# Revit family: IS_Synergy_Multiproduct_BIM_GB_L6220;L6221;L6222;L6223;L6224;L6225;L6226;L6227
name_source: partatom
category: Plumbing Fixtures
revit_build: Autodesk Revit MEP 2012 (Build: 20110309_2315(x64)
units: mm (PartAtom-declared; Revit-internal decimal feet)

## types (8) — shared parameters
Accessories = www.idealspec.co.uk
AreaUnits = millimeters
Assembly Code = C1030200
AssetType = Fixed
BREEAM = No
Brand = Ideal Standard
CodePerformance = EN 14428:2004
EN 14428:2004
Color = Silver, clear
Default Elevation = 1219 mm
DurationUnit = year
ECA = No
ExpectedLife = 30
Features = Idealclean clear glass, bright silver finish
Finish = Clear, silver
FrameMatl = ISI_IdealStandard_Shower_BrightSilver_Render
GlazingMatl = ISI_IdealStandard_Shower_Glass_Render
IfcExportAs = IfcFurnitureType
IfcExportType = USERDEFINED
InstallationInstructions = www.idealspec.co.uk/resources.html
LinearUnits = millimeters
MainColor = Silver, clear
ManufacturerURL = www.idealspec.co.uk
Material = Glass, aluminium
NBSDescription = Shower enclosures
NBSReference = 45-35-70/332
NominalHeight = 2000 mm  [stored 6.56168 ft]
Shape = Rectangular
Space = Internal
SpareParts = www.fastpart-spares.co.uk
TMV3 = No
URL = www.idealspec.co.uk
Uniclass2 = Pr_40_20_06_79
Version = 1
VolumeUnits = Litres
WRAS = No
WarrantyDescription = Manufacturers warranty
WarrantyDurationParts = 10
WarrantyDurationUnit = year
WaterEfficientProduct = No

## per-type parameters (varying)
| type | BIMObjectName | Description | Model | ModelNumber | ModelReference | Name | NettWeight | NominalDepth | NominalDepthActual | NominalLength | NominalWidth | ProductInformation | Size |
| L6220EO - Synergy wet room panel 700 mm | ISI_IdealStandard_Showers_Synergy-WetRoomPanel_L6220EO | Synergy 700 mm wet room panel | L6220EO | L6220EO | Synergy 700 mm wet room panel | Showers_Synergy-WetRoomPanel_L6220EO_IdealStandard | 26.9 Kg | 700 mm  [stored 2.29659 ft] | 700 mm  [stored 2.29659 ft] | 700 mm  [stored 2.29659 ft] | 700 mm  [stored 2.29659 ft] | www.idealspec.co.uk/datasheets/L6220EO | 2025 x 700 x 50mm |
| L6221EO - Synergy wet room panel 760 mm | ISI_IdealStandard_Showers_Synergy-WetRoomPanel_L6221EO | Synergy 760 mm wet room panel | L6221EO | L6221EO | Synergy 760 mm wet room panel | Showers_Synergy-WetRoomPanel_L6221EO_IdealStandard | 32 Kg | 760 mm | 760 mm | 760 mm | 760 mm | www.idealspec.co.uk/datasheets/L6221EO | 2025 x 760 x 50mm |
| L6222EO - Synergy wet room panel 800 mm | ISI_IdealStandard_Showers_Synergy-WetRoomPanel_L6222EO | Synergy 800 mm wet room panel | L6222EO | L6222EO | Synergy 800 mm wet room panel | Showers_Synergy-WetRoomPanel_L6222EO_IdealStandard | 34 Kg | 800 mm  [stored 2.62467 ft] | 800 mm  [stored 2.62467 ft] | 800 mm  [stored 2.62467 ft] | 800 mm  [stored 2.62467 ft] | www.idealspec.co.uk/datasheets/L6222EO | 2025 x 800 x 50mm |
| L6223EO - Synergy wet room panel 900 mm | ISI_IdealStandard_Showers_Synergy-WetRoomPanel_L6223EO | Synergy 900 mm wet room panel | L6223EO | L6223EO | Synergy 900 mm wet room panel | Showers_Synergy-WetRoomPanel_L6223EO_IdealStandard | 37 Kg | 900 mm  [stored 2.95276 ft] | 900 mm  [stored 2.95276 ft] | 900 mm  [stored 2.95276 ft] | 900 mm  [stored 2.95276 ft] | www.idealspec.co.uk/datasheets/L6223EO | 2025 x 900 x 50mm |
| L6224EO - Synergy wet room panel 1000 mm | ISI_IdealStandard_Showers_Synergy-WetRoomPanel_L6224EO | Synergy 1000 mm wet room panel | L6224EO | L6224EO | Synergy 1000 mm wet room panel | Showers_Synergy-WetRoomPanel_L6224EO_IdealStandard | 42 Kg | 900 mm  [stored 2.95276 ft] | 900 mm  [stored 2.95276 ft] | 900 mm  [stored 2.95276 ft] | 1000 mm  [stored 3.28084 ft] | www.idealspec.co.uk/datasheets/L6224EO | 2025 x 1000 x 50mm |
| L6225EO - Synergy wet room panel 1200 mm | ISI_IdealStandard_Showers_Synergy-WetRoomPanel_L6225EO | Synergy 1200 mm wet room panel | L6225EO | L6225EO | Synergy 1200 mm wet room panel | Showers_Synergy-WetRoomPanel_L6225EO_IdealStandard | 42 Kg | 900 mm  [stored 2.95276 ft] | 900 mm  [stored 2.95276 ft] | 900 mm  [stored 2.95276 ft] | 1200 mm | www.idealspec.co.uk/datasheets/L6225EO | 2025 x 1200 x 50mm |
| L6226EO - Synergy wet room panel 1400 mm | ISI_IdealStandard_Showers_Synergy-WetRoomPanel_L6226EO | Synergy 1400 mm wet room panel | L6226EO | L6226EO | Synergy 1400 mm wet room panel | Showers_Synergy-WetRoomPanel_L6226EO_IdealStandard | 61 Kg | 900 mm  [stored 2.95276 ft] | 900 mm  [stored 2.95276 ft] | 900 mm  [stored 2.95276 ft] | 1400 mm  [stored 4.59318 ft] | www.idealspec.co.uk/datasheets/L6226EO | 2025 x 1400 x 50mm |
| L6227EO - Synergy wet room panel 1600 mm | ISI_IdealStandard_Showers_Synergy-WetRoomPanel_L6227EO | Synergy 1600 mm wet room panel | L6227EO | L6227EO | Synergy 1600 mm wet room panel | Showers_Synergy-WetRoomPanel_L6227EO_IdealStandard | 68 Kg | 900 mm  [stored 2.95276 ft] | 900 mm  [stored 2.95276 ft] | 900 mm  [stored 2.95276 ft] | 1600 mm  [stored 5.24934 ft] | www.idealspec.co.uk/datasheets/L6227EO | 2025 x 1600 x 50mm |

note: [stored X ft] marks values corroborated as IEEE doubles in the binary element streams (Revit-internal decimal feet)

## geometry (parser evidence)
native form markers: Blend x2, Sweep x3
no freeform markers — native parametric forms only
